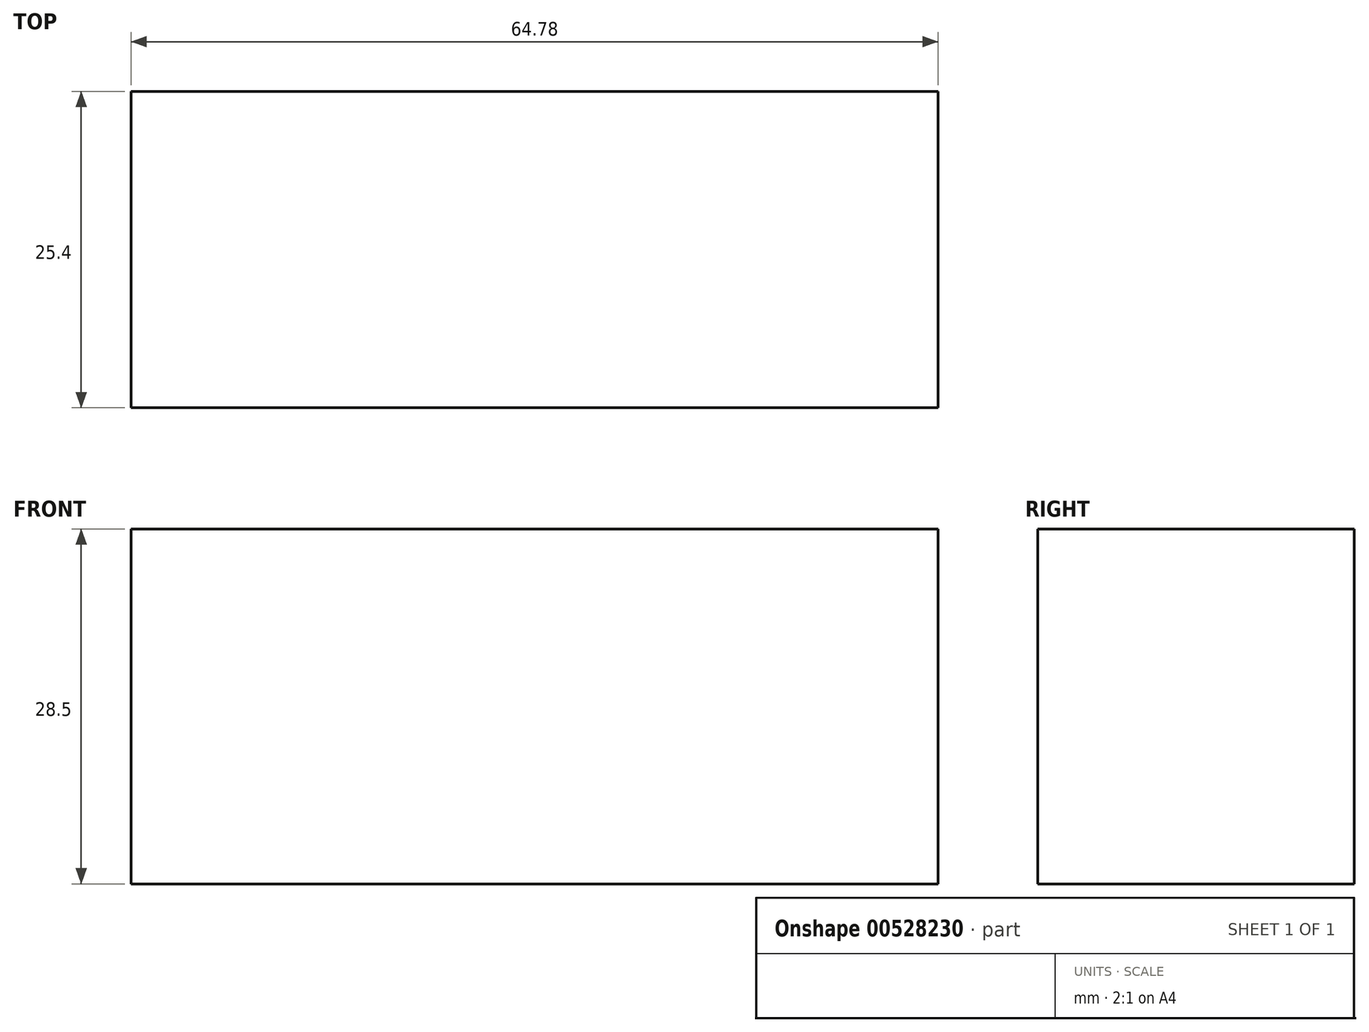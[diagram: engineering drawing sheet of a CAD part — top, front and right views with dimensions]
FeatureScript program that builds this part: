
annotation { "Feature Type Name" : "Feature", "Feature Type Description" : "" }
export const myFeature = defineFeature(function(context is Context, id is Id, definition is map)
    precondition{}
    {
        {
            var Q0;
            Q0=qCreatedBy(makeId("Front.planeOp"),FACE);
            var sketch = newSketch(context, id + "F0", { "sketchPlane" : qUnion([Q0])});
            skLineSegment(sketch, "E0.bottom", {"start": v(-34.98, 27.2) * mm, "end": v(29.8, 27.2) * mm});
            skLineSegment(sketch, "E0.top", {"start": v(-34.98, 55.7) * mm, "end": v(29.8, 55.7) * mm});
            skLineSegment(sketch, "E0.left", {"start": v(-34.98, 27.2) * mm, "end": v(-34.98, 55.7) * mm});
            skLineSegment(sketch, "E0.right", {"start": v(29.8, 27.2) * mm, "end": v(29.8, 55.7) * mm});
            skSolve(sketch);
        }
        {
            var Q0;
            Q0=makeQuery(id+"F0.imprint","IMPRINT",FACE,{"disambiguationData":[TD([[makeQuery(id+"F0.imprint","IMPRINT",EDGE,{"derivedFrom":sQuery(id+"F0.wireOp",EDGE,"E0.bottom")}),1.0]])]});
            extrude(context, id + "F1", {"entities" : qUnion([Q0]), "depth" : 25.4 * mm, "offsetDistance" : 25.4 * mm});
        }
    });
